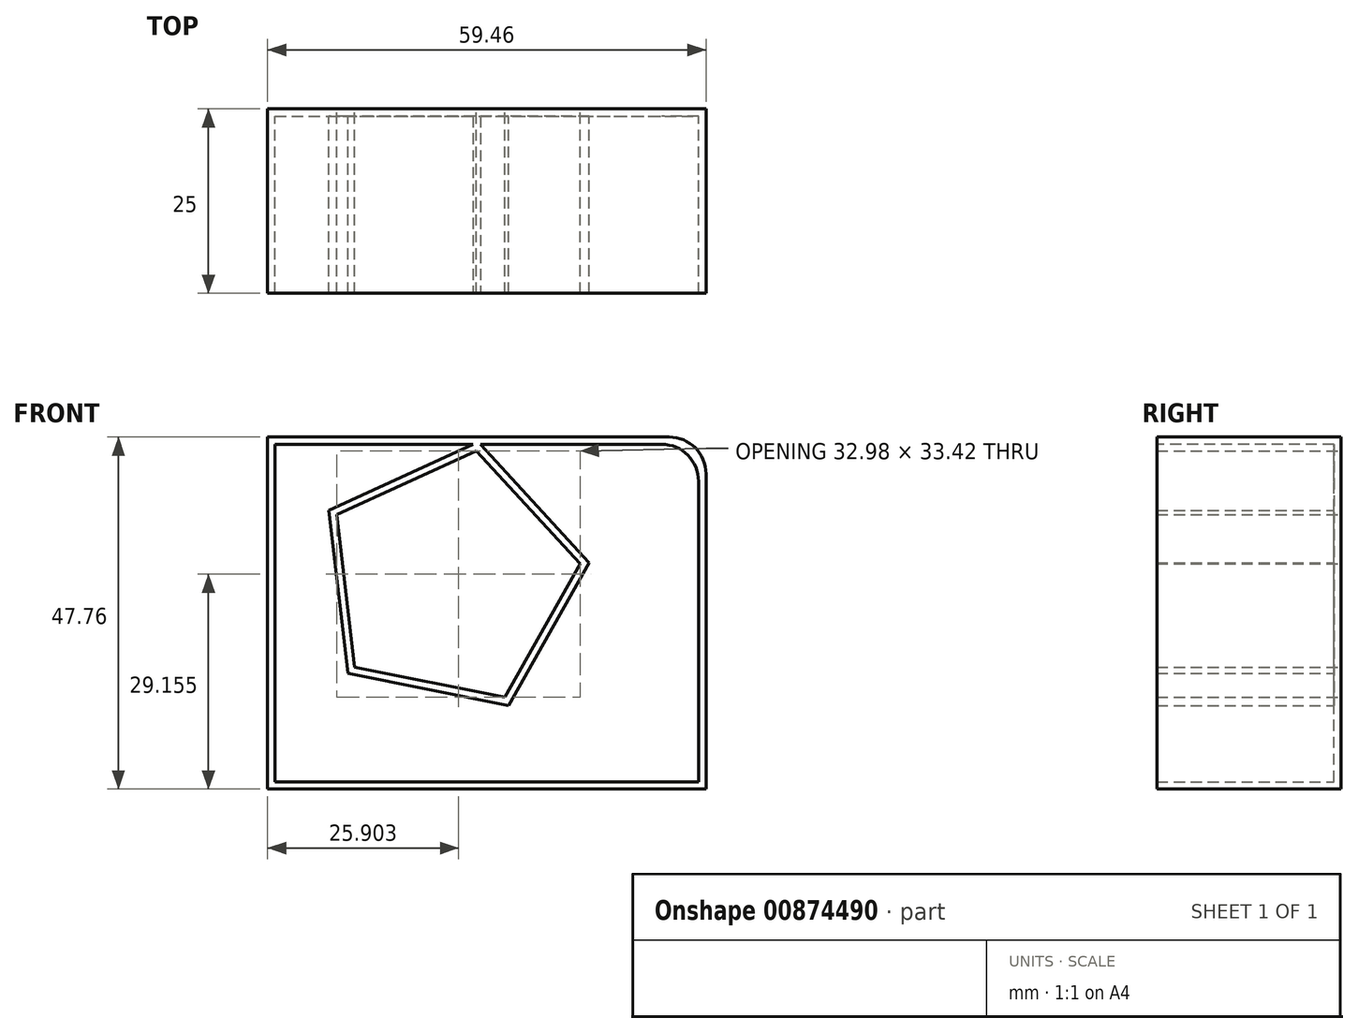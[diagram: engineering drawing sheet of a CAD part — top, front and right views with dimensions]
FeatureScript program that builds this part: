
annotation { "Feature Type Name" : "Feature", "Feature Type Description" : "" }
export const myFeature = defineFeature(function(context is Context, id is Id, definition is map)
    precondition{}
    {
        {
            var Q0;
            Q0=qCreatedBy(makeId("Front.planeOp"),FACE);
            var sketch = newSketch(context, id + "F0", { "sketchPlane" : qUnion([Q0])});
            skLineSegment(sketch, "E0.bottom", {"start": v(0, 0) * mm, "end": v(59.46, 0) * mm});
            skLineSegment(sketch, "E0.top", {"start": v(0, 47.76) * mm, "end": v(59.46, 47.76) * mm});
            skLineSegment(sketch, "E0.left", {"start": v(0, 0) * mm, "end": v(0, 47.76) * mm});
            skLineSegment(sketch, "E0.right", {"start": v(59.46, 0) * mm, "end": v(59.46, 47.76) * mm});
            skCircle(sketch, "E1.cCircle", {"center": v(24.82, 28.53) * mm, "radius": 14.31 * mm, "construction": true});
            skLineSegment(sketch, "E1.0", {"start": v(42.4, 30.56) * mm, "end": v(32.2, 12.44) * mm});
            skLineSegment(sketch, "E1.1", {"start": v(32.2, 12.44) * mm, "end": v(11.8, 16.55) * mm});
            skLineSegment(sketch, "E1.2", {"start": v(11.8, 16.55) * mm, "end": v(9.41, 37.2) * mm});
            skLineSegment(sketch, "E1.3", {"start": v(9.41, 37.2) * mm, "end": v(28.32, 45.87) * mm});
            skLineSegment(sketch, "E1.4", {"start": v(28.32, 45.87) * mm, "end": v(42.4, 30.56) * mm});
            skPoint(sketch, "E1.0.midPoint", {"position": v(37.3, 21.5) * mm});
            skSolve(sketch);
        }
        {
            var Q0;
            Q0=makeQuery(id+"F0.imprint","IMPRINT",FACE,{"disambiguationData":[TD([[makeQuery(id+"F0.imprint","IMPRINT",EDGE,{"derivedFrom":sQuery(id+"F0.wireOp",EDGE,"E0.bottom")}),1.0]])]});
            extrude(context, id + "F1", {"entities" : qUnion([Q0]), "depth" : 25 * mm, "offsetDistance" : 25 * mm});
        }
        {
            var Q0;
            Q0=makeQuery(id+"F1.opExtrude","CAP_FACE",FACE,{"disambiguationData":[OSD([sQuery(id+"F0.wireOp",EDGE,"E0.bottom"),sQuery(id+"F0.wireOp",EDGE,"E0.top"),sQuery(id+"F0.wireOp",EDGE,"E0.left"),sQuery(id+"F0.wireOp",EDGE,"E0.right"),sQuery(id+"F0.wireOp",EDGE,"E1.0"),sQuery(id+"F0.wireOp",EDGE,"E1.1"),sQuery(id+"F0.wireOp",EDGE,"E1.2"),sQuery(id+"F0.wireOp",EDGE,"E1.3"),sQuery(id+"F0.wireOp",EDGE,"E1.4")])],"isStart":false});
            shell(context, id + "F2", {"entities" : qUnion([Q0]), "thickness" : 1 * mm});
        }
        {
            var Q0;
            Q0=makeQuery(id+"F2.opShell","OFFSET_EDGE",EDGE,{"disambiguationData":[OSD([sQuery(id+"F0.wireOp",EDGE,"E0.top"),sQuery(id+"F0.wireOp",EDGE,"E0.right")])]});
            var Q1;
            Q1=makeQuery(id+"F1.opExtrude","SWEPT_EDGE",EDGE,{"disambiguationData":[OSD([sQuery(id+"F0.wireOp",EDGE,"E0.top"),sQuery(id+"F0.wireOp",EDGE,"E0.right")])]});
            fillet(context, id + "F3", {"entities" : qUnion([Q0, Q1]), "radius" : 5 * mm, "tangentPropagation" : true, "allowEdgeOverflow" : false});
        }
    });
